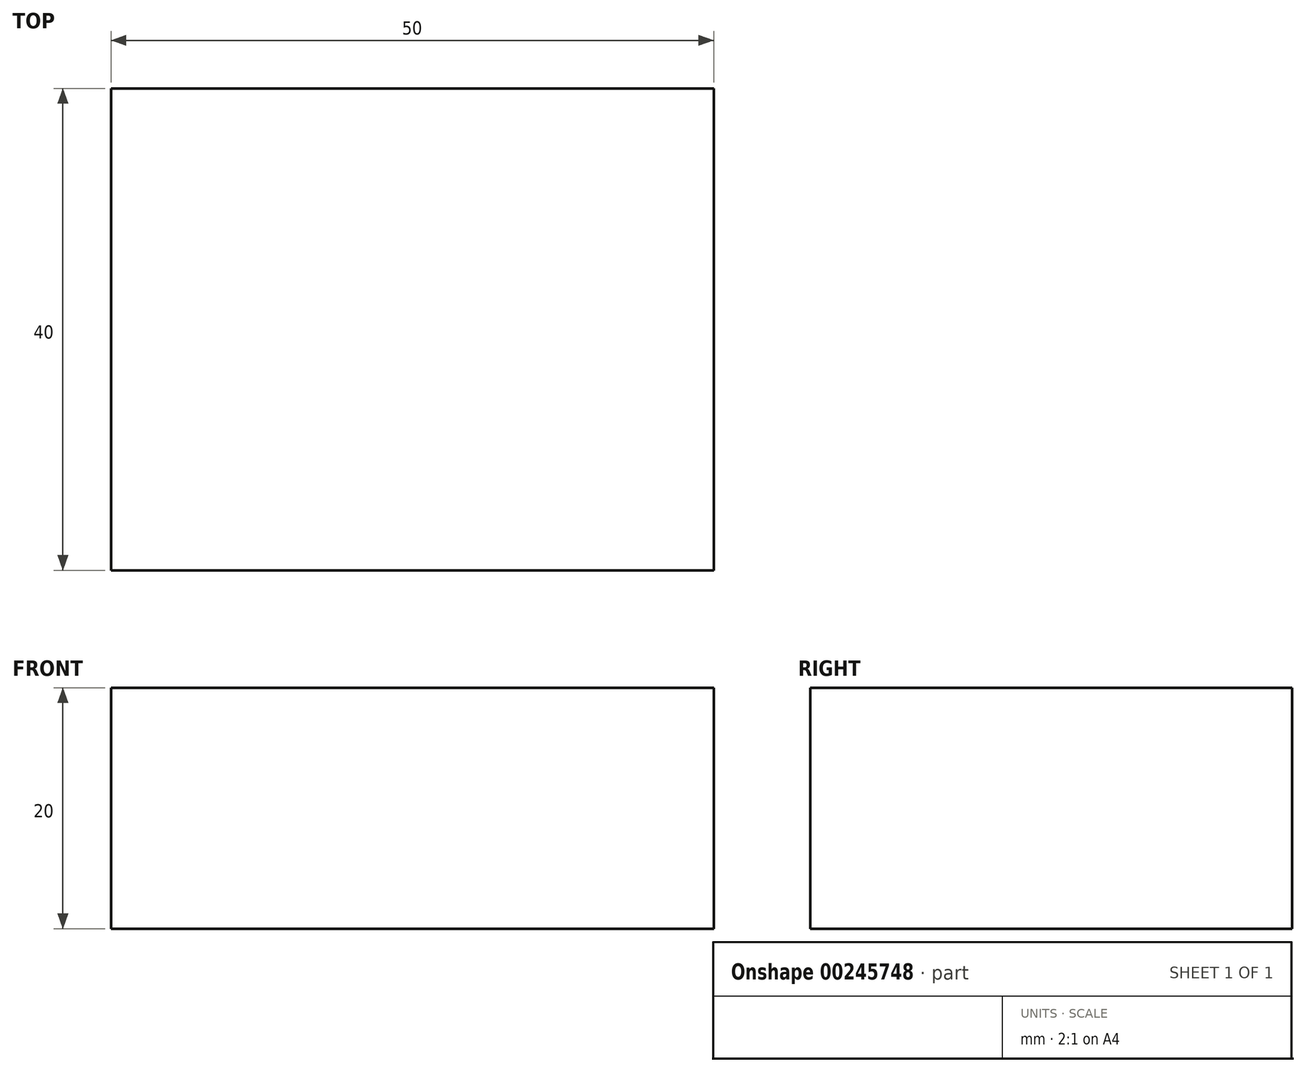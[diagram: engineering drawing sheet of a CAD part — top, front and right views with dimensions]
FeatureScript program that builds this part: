
annotation { "Feature Type Name" : "Feature", "Feature Type Description" : "" }
export const myFeature = defineFeature(function(context is Context, id is Id, definition is map)
    precondition{}
    {
        {
            var Q0;
            Q0=qCreatedBy(makeId("Top.planeOp"),FACE);
            var sketch = newSketch(context, id + "F0", { "sketchPlane" : qUnion([Q0])});
            skLineSegment(sketch, "E0.bottom", {"start": v(0, 0) * mm, "end": v(50, 0) * mm});
            skLineSegment(sketch, "E0.top", {"start": v(0, 40) * mm, "end": v(50, 40) * mm});
            skLineSegment(sketch, "E0.left", {"start": v(0, 0) * mm, "end": v(0, 40) * mm});
            skLineSegment(sketch, "E0.right", {"start": v(50, 0) * mm, "end": v(50, 40) * mm});
            skSolve(sketch);
        }
        {
            var Q0;
            Q0=makeQuery(id+"F0.imprint","IMPRINT",FACE,{"disambiguationData":[TD([[makeQuery(id+"F0.imprint","IMPRINT",EDGE,{"derivedFrom":sQuery(id+"F0.wireOp",EDGE,"E0.bottom")}),1.0]])]});
            extrude(context, id + "F1", {"entities" : qUnion([Q0]), "depth" : 20 * mm});
        }
    });
